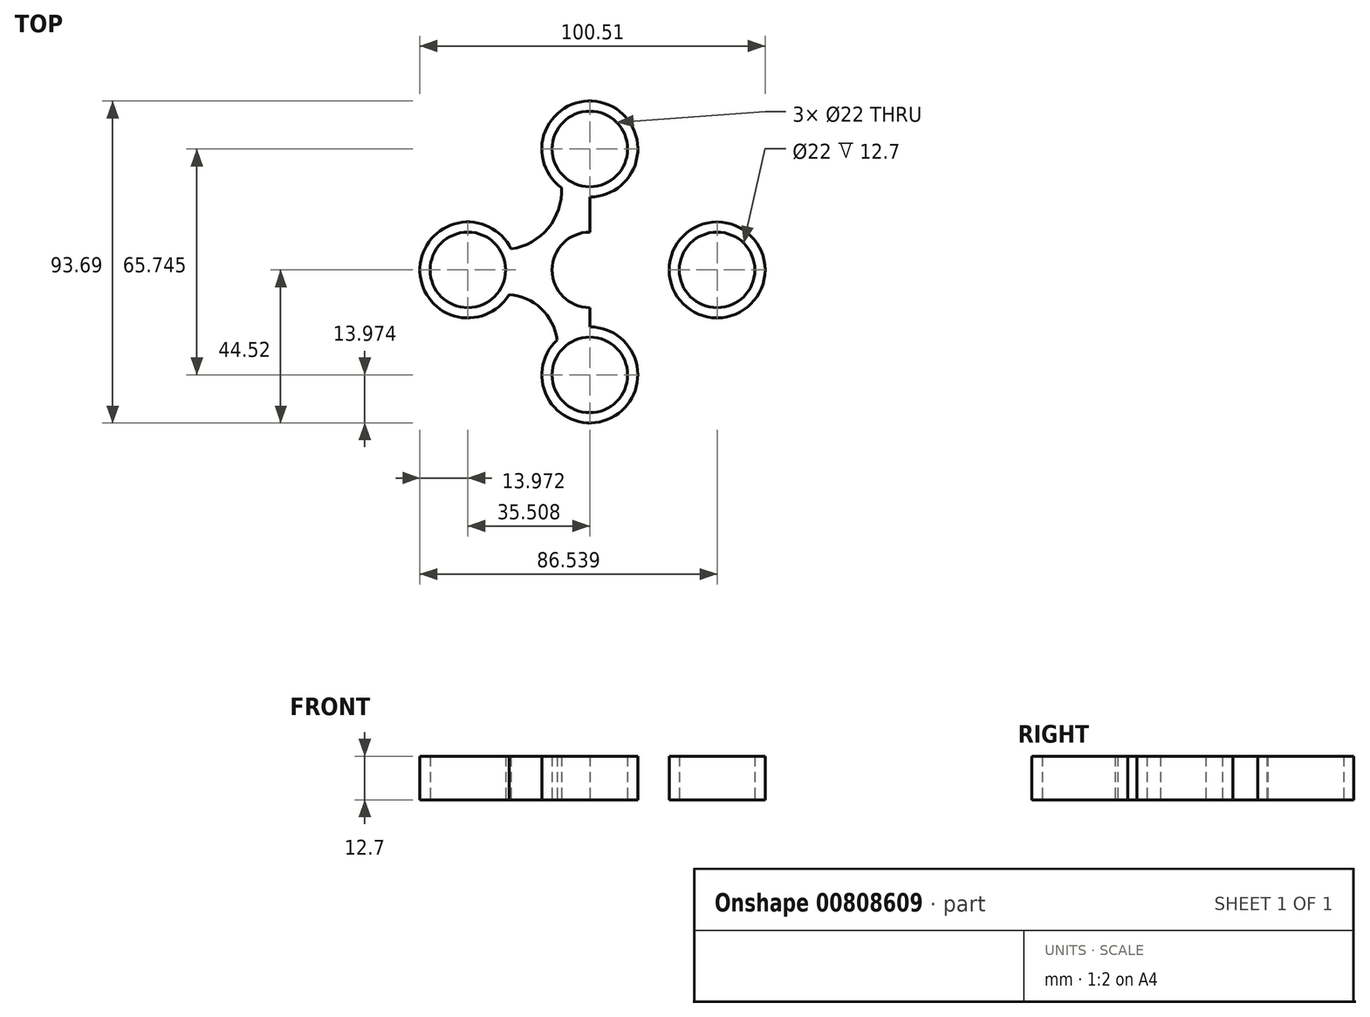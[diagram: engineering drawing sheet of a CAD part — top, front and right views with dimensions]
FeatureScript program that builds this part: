
annotation { "Feature Type Name" : "Feature", "Feature Type Description" : "" }
export const myFeature = defineFeature(function(context is Context, id is Id, definition is map)
    precondition{}
    {
        {
            var Q0;
            Q0=qCreatedBy(makeId("Top.planeOp"),FACE);
            var sketch = newSketch(context, id + "F0", { "sketchPlane" : qUnion([Q0])});
            skCircle(sketch, "E0", {"center": v(0, 0) * mm, "radius": 57.15 * mm});
            skCircle(sketch, "E1", {"center": v(0, 0) * mm, "radius": 11 * mm});
            skCircle(sketch, "E2", {"center": v(-35.5, 0) * mm, "radius": 11 * mm});
            skCircle(sketch, "E3", {"center": v(37.06, 0) * mm, "radius": 11 * mm});
            skCircle(sketch, "E4", {"center": v(0, 35.2) * mm, "radius": 11 * mm});
            skCircle(sketch, "E5", {"center": v(0, -30.55) * mm, "radius": 11 * mm});
            skLineSegment(sketch, "E6", {"start": v(-24.51, 0) * mm, "end": v(26.06, 0) * mm});
            skLineSegment(sketch, "E7", {"start": v(0, 24.2) * mm, "end": v(0, -19.55) * mm});
            skArc(sketch, "E8", {"start": v(-26.28, 5.99) * mm, "mid": v(-11.22, 13.39) * mm, "end": v(-9.75, 30.1) * mm});
            skArc(sketch, "E9", {"start": v(9.75, 30.1) * mm, "mid": v(14.7, 13.9) * mm, "end": v(30.96, 9.16) * mm});
            skArc(sketch, "E10", {"start": v(-9.75, -25.45) * mm, "mid": v(-13.72, -11.72) * mm, "end": v(-27.33, -7.36) * mm});
            skArc(sketch, "E11", {"start": v(28.45, -6.84) * mm, "mid": v(15.13, -11.55) * mm, "end": v(9.06, -24.31) * mm});
            skCircle(sketch, "E12", {"center": v(0, 35.2) * mm, "radius": 13.97 * mm});
            skCircle(sketch, "E13", {"center": v(-35.5, 0) * mm, "radius": 13.97 * mm});
            skCircle(sketch, "E14", {"center": v(37.06, 0) * mm, "radius": 13.97 * mm});
            skCircle(sketch, "E15", {"center": v(0, -30.55) * mm, "radius": 13.97 * mm});
            skCircle(sketch, "E16", {"center": v(0, 0) * mm, "radius": 13.97 * mm});
            skSolve(sketch);
        }
        {
            var Q0;
            {var subQ0=sQuery(id+"F0.wireOp",EDGE,"E8");var subQ1=sQuery(id+"F0.wireOp",EDGE,"E2");var subQ2=makeQuery(id+"F0.imprint","INTERSECT",VERTEX,{"derivedFrom":[subQ1,subQ0]});Q0=makeQuery(id+"F0.imprint","IMPRINT",FACE,{"disambiguationData":[TD([[makeQuery(id+"F0.imprint","IMPRINT",EDGE,{"disambiguationData":[TD([[subQ2,-1.0]])],"derivedFrom":subQ1}),-1.0]])]});}
            var Q1;
            {var subQ0=sQuery(id+"F0.wireOp",EDGE,"E6");var subQ1=sQuery(id+"F0.wireOp",EDGE,"E2");var subQ2=makeQuery(id+"F0.imprint","INTERSECT",VERTEX,{"derivedFrom":[subQ1,subQ0]});Q1=makeQuery(id+"F0.imprint","IMPRINT",FACE,{"disambiguationData":[TD([[makeQuery(id+"F0.imprint","IMPRINT",EDGE,{"disambiguationData":[TD([[subQ2,-1.0]])],"derivedFrom":subQ1}),-1.0]])]});}
            var Q2;
            {var subQ0=sQuery(id+"F0.wireOp",EDGE,"E6");var subQ1=sQuery(id+"F0.wireOp",EDGE,"E2");var subQ2=makeQuery(id+"F0.imprint","INTERSECT",VERTEX,{"derivedFrom":[subQ1,subQ0]});Q2=makeQuery(id+"F0.imprint","IMPRINT",FACE,{"disambiguationData":[TD([[makeQuery(id+"F0.imprint","IMPRINT",EDGE,{"disambiguationData":[TD([[subQ2,1.0]])],"derivedFrom":subQ1}),-1.0]])]});}
            var Q3;
            {var subQ5=sQuery(id+"F0.wireOp",EDGE,"E13");var subQ9=sQuery(id+"F0.wireOp",EDGE,"E6");var subQ10=makeQuery(id+"F0.imprint","INTERSECT",VERTEX,{"derivedFrom":[subQ9,subQ5]});Q3=makeQuery(id+"F0.imprint","IMPRINT",FACE,{"disambiguationData":[TD([[makeQuery(id+"F0.imprint","IMPRINT",EDGE,{"disambiguationData":[TD([[subQ10,-1.0]])],"derivedFrom":subQ9}),1.0]])]});}
            var Q4;
            {var subQ0=sQuery(id+"F0.wireOp",EDGE,"E13");var subQ1=sQuery(id+"F0.wireOp",EDGE,"E6");var subQ2=makeQuery(id+"F0.imprint","INTERSECT",VERTEX,{"derivedFrom":[subQ1,subQ0]});Q4=makeQuery(id+"F0.imprint","IMPRINT",FACE,{"disambiguationData":[TD([[makeQuery(id+"F0.imprint","IMPRINT",EDGE,{"disambiguationData":[TD([[subQ2,-1.0]])],"derivedFrom":subQ1}),-1.0]])]});}
            var Q5;
            {var subQ0=sQuery(id+"F0.wireOp",EDGE,"E10");var subQ1=sQuery(id+"F0.wireOp",EDGE,"E5");var subQ2=makeQuery(id+"F0.imprint","INTERSECT",VERTEX,{"derivedFrom":[subQ1,subQ0]});Q5=makeQuery(id+"F0.imprint","IMPRINT",FACE,{"disambiguationData":[TD([[makeQuery(id+"F0.imprint","IMPRINT",EDGE,{"disambiguationData":[TD([[subQ2,-1.0]])],"derivedFrom":subQ1}),-1.0]])]});}
            var Q6;
            {var subQ0=sQuery(id+"F0.wireOp",EDGE,"E7");var subQ1=sQuery(id+"F0.wireOp",EDGE,"E5");var subQ2=makeQuery(id+"F0.imprint","INTERSECT",VERTEX,{"derivedFrom":[subQ1,subQ0]});Q6=makeQuery(id+"F0.imprint","IMPRINT",FACE,{"disambiguationData":[TD([[makeQuery(id+"F0.imprint","IMPRINT",EDGE,{"disambiguationData":[TD([[subQ2,1.0]])],"derivedFrom":subQ1}),-1.0]])]});}
            var Q7;
            {var subQ0=sQuery(id+"F0.wireOp",EDGE,"E7");var subQ1=sQuery(id+"F0.wireOp",EDGE,"E5");var subQ2=makeQuery(id+"F0.imprint","INTERSECT",VERTEX,{"derivedFrom":[subQ1,subQ0]});Q7=makeQuery(id+"F0.imprint","IMPRINT",FACE,{"disambiguationData":[TD([[makeQuery(id+"F0.imprint","IMPRINT",EDGE,{"disambiguationData":[TD([[subQ2,-1.0]])],"derivedFrom":subQ1}),-1.0]])]});}
            var Q8;
            {var subQ1=sQuery(id+"F0.wireOp",EDGE,"E6");var subQ5=sQuery(id+"F0.wireOp",EDGE,"E16");var subQ11=makeQuery(id+"F0.imprint","INTERSECT",VERTEX,{"disambiguationData":[OD(1.0)],"derivedFrom":[subQ1,subQ5]});Q8=makeQuery(id+"F0.imprint","IMPRINT",FACE,{"disambiguationData":[TD([[makeQuery(id+"F0.imprint","IMPRINT",EDGE,{"disambiguationData":[TD([[subQ11,-1.0]])],"derivedFrom":subQ1}),-1.0]])]});}
            var Q9;
            {var subQ0=sQuery(id+"F0.wireOp",EDGE,"E9");var subQ1=sQuery(id+"F0.wireOp",EDGE,"E3");var subQ2=makeQuery(id+"F0.imprint","INTERSECT",VERTEX,{"derivedFrom":[subQ1,subQ0]});Q9=makeQuery(id+"F0.imprint","IMPRINT",FACE,{"disambiguationData":[TD([[makeQuery(id+"F0.imprint","IMPRINT",EDGE,{"disambiguationData":[TD([[subQ2,1.0]])],"derivedFrom":subQ1}),-1.0]])]});}
            var Q10;
            {var subQ0=sQuery(id+"F0.wireOp",EDGE,"E6");var subQ1=sQuery(id+"F0.wireOp",EDGE,"E3");var subQ2=makeQuery(id+"F0.imprint","INTERSECT",VERTEX,{"derivedFrom":[subQ1,subQ0]});Q10=makeQuery(id+"F0.imprint","IMPRINT",FACE,{"disambiguationData":[TD([[makeQuery(id+"F0.imprint","IMPRINT",EDGE,{"disambiguationData":[TD([[subQ2,1.0]])],"derivedFrom":subQ1}),-1.0]])]});}
            var Q11;
            {var subQ0=sQuery(id+"F0.wireOp",EDGE,"E6");var subQ1=sQuery(id+"F0.wireOp",EDGE,"E3");var subQ2=makeQuery(id+"F0.imprint","INTERSECT",VERTEX,{"derivedFrom":[subQ1,subQ0]});Q11=makeQuery(id+"F0.imprint","IMPRINT",FACE,{"disambiguationData":[TD([[makeQuery(id+"F0.imprint","IMPRINT",EDGE,{"disambiguationData":[TD([[subQ2,-1.0]])],"derivedFrom":subQ1}),-1.0]])]});}
            var Q12;
            {var subQ7=sQuery(id+"F0.wireOp",EDGE,"E16");var subQ9=sQuery(id+"F0.wireOp",EDGE,"E6");var subQ10=makeQuery(id+"F0.imprint","INTERSECT",VERTEX,{"disambiguationData":[OD(1.0)],"derivedFrom":[subQ9,subQ7]});Q12=makeQuery(id+"F0.imprint","IMPRINT",FACE,{"disambiguationData":[TD([[makeQuery(id+"F0.imprint","IMPRINT",EDGE,{"disambiguationData":[TD([[subQ10,-1.0]])],"derivedFrom":subQ9}),1.0]])]});}
            var Q13;
            {var subQ0=sQuery(id+"F0.wireOp",EDGE,"E8");var subQ1=sQuery(id+"F0.wireOp",EDGE,"E4");var subQ2=makeQuery(id+"F0.imprint","INTERSECT",VERTEX,{"derivedFrom":[subQ1,subQ0]});Q13=makeQuery(id+"F0.imprint","IMPRINT",FACE,{"disambiguationData":[TD([[makeQuery(id+"F0.imprint","IMPRINT",EDGE,{"disambiguationData":[TD([[subQ2,1.0]])],"derivedFrom":subQ1}),-1.0]])]});}
            var Q14;
            {var subQ0=sQuery(id+"F0.wireOp",EDGE,"E7");var subQ1=sQuery(id+"F0.wireOp",EDGE,"E4");var subQ2=makeQuery(id+"F0.imprint","INTERSECT",VERTEX,{"derivedFrom":[subQ1,subQ0]});Q14=makeQuery(id+"F0.imprint","IMPRINT",FACE,{"disambiguationData":[TD([[makeQuery(id+"F0.imprint","IMPRINT",EDGE,{"disambiguationData":[TD([[subQ2,-1.0]])],"derivedFrom":subQ1}),-1.0]])]});}
            var Q15;
            {var subQ0=sQuery(id+"F0.wireOp",EDGE,"E7");var subQ1=sQuery(id+"F0.wireOp",EDGE,"E4");var subQ2=makeQuery(id+"F0.imprint","INTERSECT",VERTEX,{"derivedFrom":[subQ1,subQ0]});Q15=makeQuery(id+"F0.imprint","IMPRINT",FACE,{"disambiguationData":[TD([[makeQuery(id+"F0.imprint","IMPRINT",EDGE,{"disambiguationData":[TD([[subQ2,1.0]])],"derivedFrom":subQ1}),-1.0]])]});}
            extrude(context, id + "F1", {"entities" : qUnion([Q0, Q1, Q2, Q3, Q4, Q5, Q6, Q7, Q8, Q9, Q10, Q11, Q12, Q13, Q14, Q15]), "depth" : 12.7 * mm, "offsetDistance" : 25.4 * mm});
        }
    });
